# Revit family: Haworth_BuzziSpot_EU_PRELIMINARY
name_source: partatom
category: Furniture
revit_build: Autodesk Revit 2018 (Build: 20170223_1515(x64)
units: mm (PartAtom-declared; Revit-internal decimal feet)

## family parameters
Always vertical = Yes
Cut with Voids When Loaded = No
OmniClass Number = 23.40.70.14.64.21
OmniClass Title = Systems Furniture
Room Calculation Point = No
Shared = No
Work Plane-Based = No

## types (2) — shared parameters
Actual Depth = 47 cm
Actual Height = 50 cm
Actual Width = 47 cm
Antiskid = No
Assembly Code = E2020200
Base Finish = Haworth _ Polymer _ Undecided
Casters = Yes
Description = Haworth - BuzziSpot - Pouf
Manufacturer = Haworth
Model = P0027
Revision Number = 1
Size = Verify Final Dim. w/ Haworth
URL = https://www.haworth.com
URL - Product = https://www.haworth.com
Warranty = http://www.haworth.com
Wood Base = No

## per-type parameters (varying)
| type | 3D | Flat | Void Length |
| Spot - Flat | No | Yes | 38 cm |
| Spot - 3D | Yes | No | 127 cm |

## geometry (parser evidence)
native form markers: Sweep x2
no freeform markers — native parametric forms only
